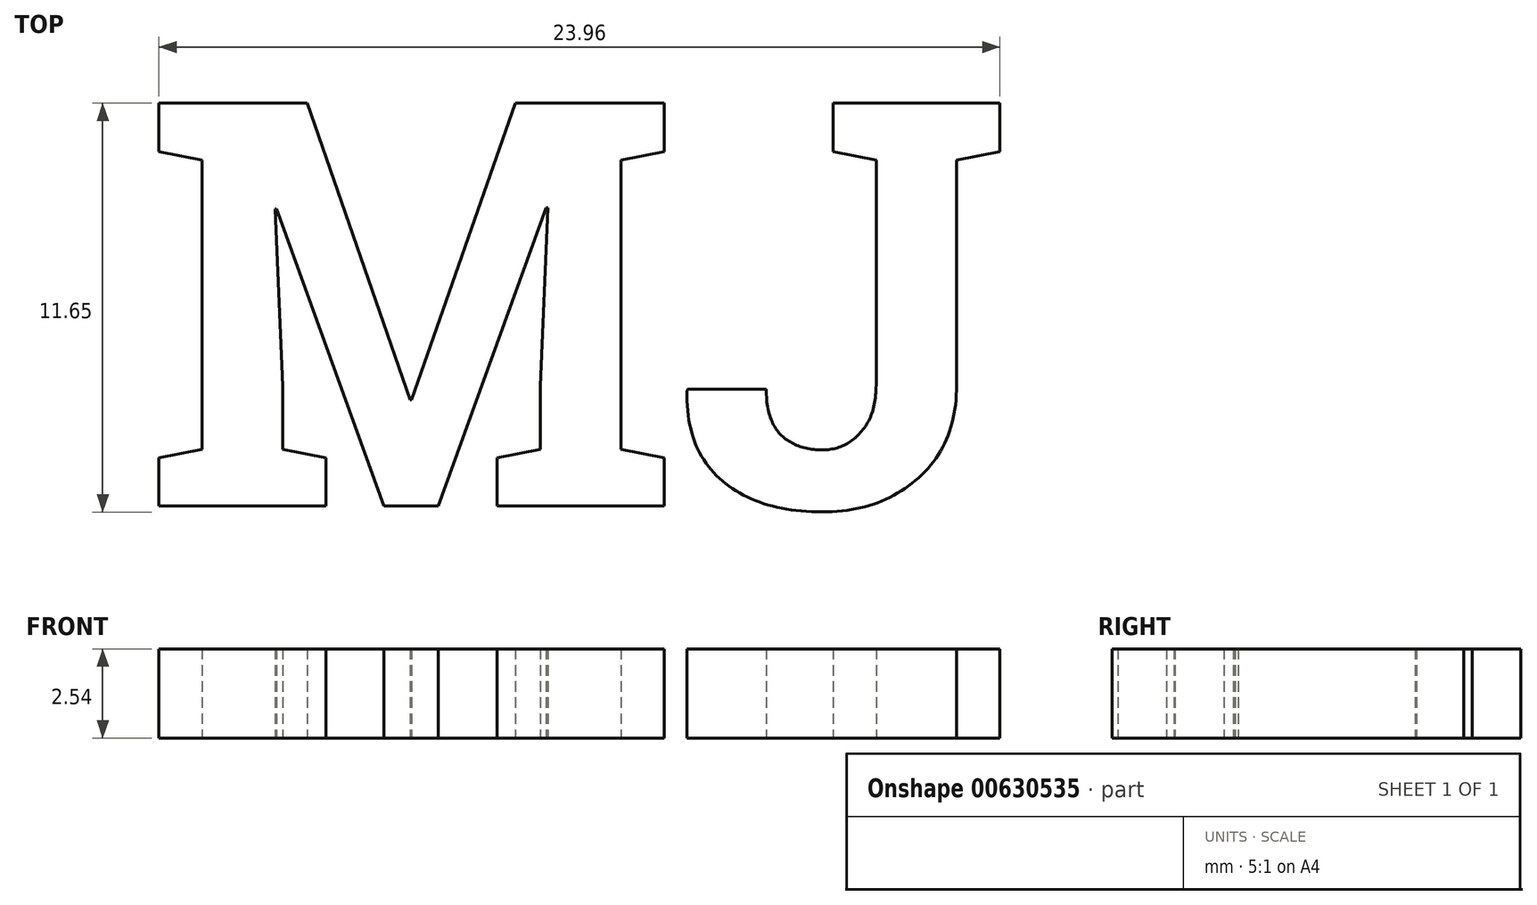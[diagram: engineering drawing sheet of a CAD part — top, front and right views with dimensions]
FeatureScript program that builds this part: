
annotation { "Feature Type Name" : "Feature", "Feature Type Description" : "" }
export const myFeature = defineFeature(function(context is Context, id is Id, definition is map)
    precondition{}
    {
        {
            var Q0;
            Q0=qCreatedBy(makeId("Top.planeOp"),FACE);
            var sketch = newSketch(context, id + "F0", { "sketchPlane" : qUnion([Q0])});
            skText(sketch, "E0", { "text": "MJ", "fontName": "RobotoSlab-Bold.ttf"});
            const initialGuessF0  = {"E0": [-0.01298, -0.00462, 1, 0, 0.01163]};
            skSetInitialGuess(sketch, initialGuessF0);
            skSolve(sketch);
        }
        {
            var Q0;
            Q0 = qSketchRegion(id + "F0", true);
            extrude(context, id + "F1", {"entities" : qUnion([Q0]), "depth" : 2.54 * mm, "offsetDistance" : 25.4 * mm});
        }
    });
